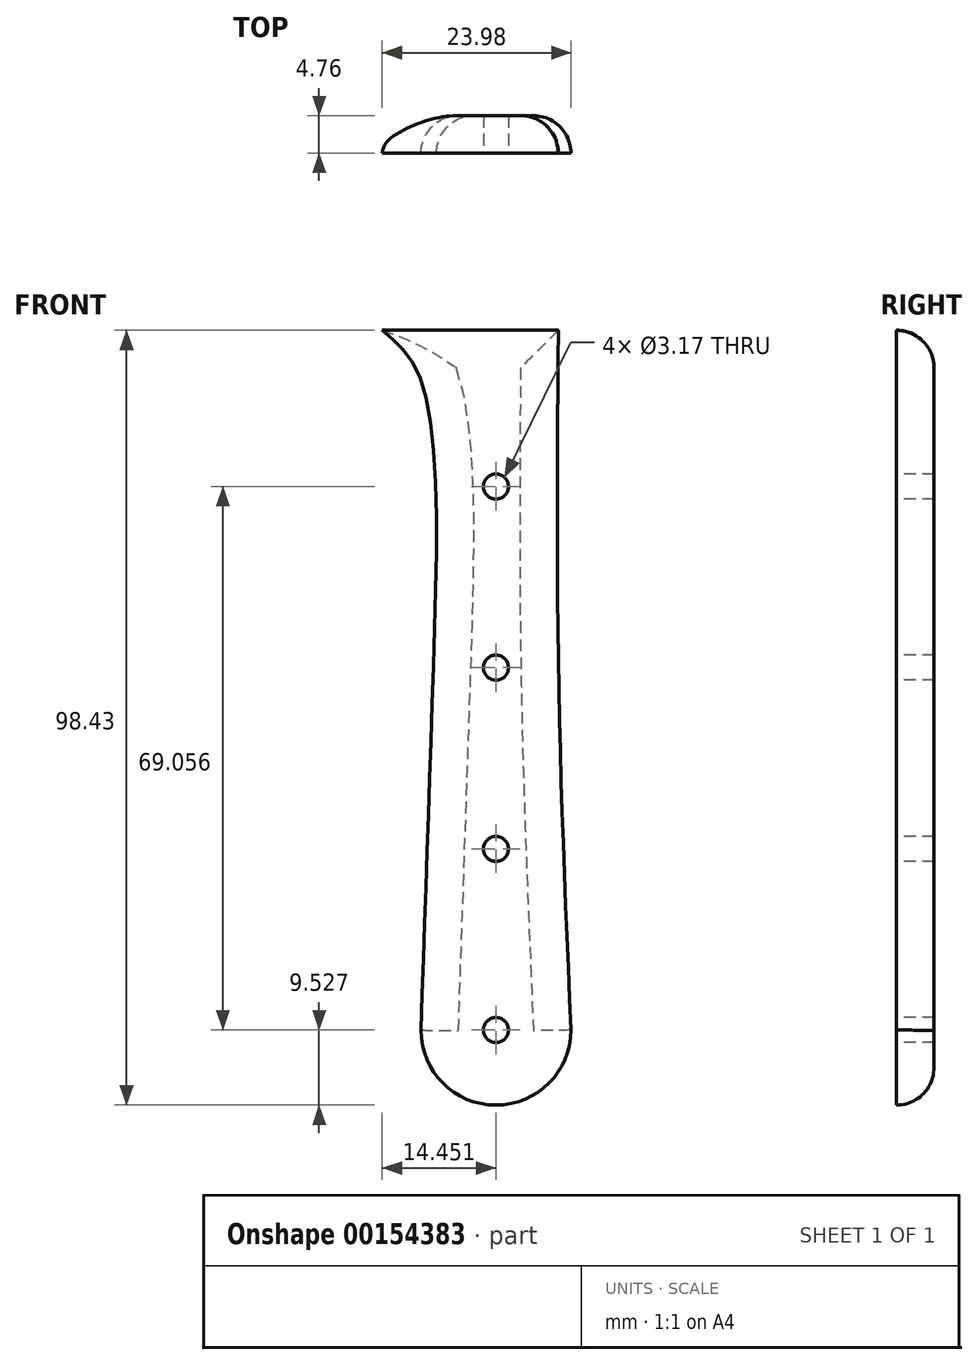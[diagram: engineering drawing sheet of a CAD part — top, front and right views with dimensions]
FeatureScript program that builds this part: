
annotation { "Feature Type Name" : "Feature", "Feature Type Description" : "" }
export const myFeature = defineFeature(function(context is Context, id is Id, definition is map)
    precondition{}
    {
        {
            var Q0;
            Q0=qCreatedBy(makeId("Front.planeOp"),FACE);
            var sketch = newSketch(context, id + "F0", { "sketchPlane" : qUnion([Q0])});
            skPoint(sketch, "E0", {"position": v(-13.22, 48.05) * mm});
            skPoint(sketch, "E1", {"position": v(9.17, 48.05) * mm});
            skLineSegment(sketch, "E2", {"start": v(-13.22, 48.05) * mm, "end": v(9.17, 48.05) * mm});
            skPoint(sketch, "E3", {"position": v(-8.3, 41.7) * mm});
            skPoint(sketch, "E4", {"position": v(-6.7, 5.18) * mm});
            skPoint(sketch, "E5", {"position": v(-8.3, -40.85) * mm});
            skPoint(sketch, "E6", {"position": v(9.17, 5.18) * mm});
            skPoint(sketch, "E7", {"position": v(10.76, -40.85) * mm});
            skPoint(sketch, "E8", {"position": v(1.23, -40.85) * mm});
            skPoint(sketch, "E9", {"position": v(1.23, -17.83) * mm});
            skPoint(sketch, "E10", {"position": v(1.23, 5.18) * mm});
            skPoint(sketch, "E11", {"position": v(1.23, 28.2) * mm});
            skFitSpline(sketch, "E12", {"points": [v(-13.22, 48.05) * mm, v(-8.3, 41.7) * mm, v(-6.7, 5.18) * mm, v(-8.3, -40.85) * mm], "startDerivative": vector(30.92, -25.24) * mm, "endDerivative": vector(-3.64, -103.8) * mm});
            skFitSpline(sketch, "E13", {"points": [v(9.17, 48.05) * mm, v(9.17, 5.18) * mm, v(10.76, -40.85) * mm], "startDerivative": vector(-0.77, -86.52) * mm, "endDerivative": vector(3.91, -91.25) * mm});
            skArc(sketch, "E14", {"start": v(-8.3, -40.85) * mm, "mid": v(1.23, -50.38) * mm, "end": v(10.76, -40.85) * mm});
            skPoint(sketch, "E15", {"position": v(1.23, -50.38) * mm});
            skSolve(sketch);
        }
        {
            var Q0;
            Q0=makeQuery(id+"F0.imprint","IMPRINT",FACE,{"disambiguationData":[TD([[makeQuery(id+"F0.imprint","IMPRINT",EDGE,{"derivedFrom":sQuery(id+"F0.wireOp",EDGE,"E2")}),-1.0]])]});
            extrude(context, id + "F1", {"entities" : qUnion([Q0]), "oppositeDirection" : true, "depth" : 4.76 * mm});
        }
        {
            var Q0;
            Q0=sQuery(id+"F0.wireOp",VERTEX,"E11");
            var Q1;
            Q1=sQuery(id+"F0.wireOp",VERTEX,"E10");
            var Q2;
            Q2=sQuery(id+"F0.wireOp",VERTEX,"E9");
            var Q3;
            Q3=sQuery(id+"F0.wireOp",VERTEX,"E8");
            var Q4;
            Q4=makeQuery(id+"F1.opExtrude","SWEPT_BODY",BODY,{"disambiguationData":[OSD([sQuery(id+"F0.wireOp",EDGE,"E2"),sQuery(id+"F0.wireOp",EDGE,"E12"),sQuery(id+"F0.wireOp",EDGE,"E13"),sQuery(id+"F0.wireOp",EDGE,"E14")])]});
            hole(context, id + "F2", {"style" : HoleStyle.SIMPLE, "endStyle" : HoleEndStyle.THROUGH, "holeDiameter" : 3.17 * mm, "locations" : qUnion([Q0, Q1, Q2, Q3]), "scope" : qUnion([Q4]), "isTappedThrough" : true});
        }
        {
            var Q0;
            Q0=makeQuery(id+"F1.opExtrude","CAP_EDGE",EDGE,{"disambiguationData":[OSD([sQuery(id+"F0.wireOp",EDGE,"E2")])],"isStart":false});
            var Q1;
            Q1=makeQuery(id+"F1.opExtrude","CAP_EDGE",EDGE,{"disambiguationData":[OSD([sQuery(id+"F0.wireOp",EDGE,"E12")])],"isStart":false});
            var Q2;
            Q2=makeQuery(id+"F1.opExtrude","CAP_EDGE",EDGE,{"disambiguationData":[OSD([sQuery(id+"F0.wireOp",EDGE,"E13")])],"isStart":false});
            var Q3;
            Q3=makeQuery(id+"F1.opExtrude","CAP_EDGE",EDGE,{"disambiguationData":[OSD([sQuery(id+"F0.wireOp",EDGE,"E14")])],"isStart":false});
            fillet(context, id + "F3", {"entities" : qUnion([Q0, Q1, Q2, Q3]), "radius" : 4.76 * mm, "tangentPropagation" : true, "allowEdgeOverflow" : false});
        }
    });
